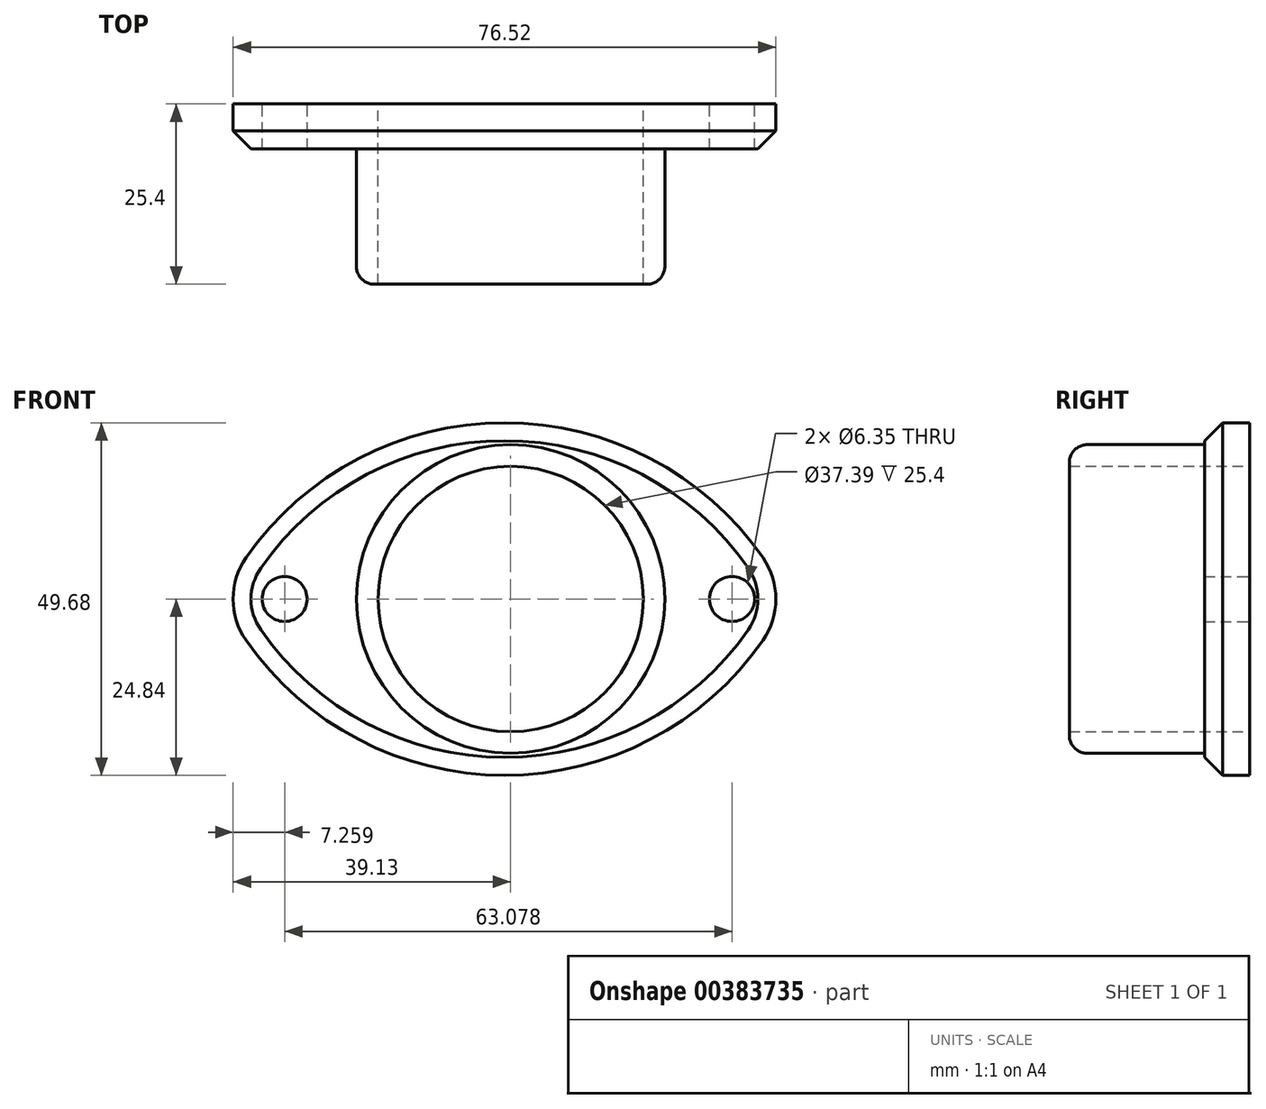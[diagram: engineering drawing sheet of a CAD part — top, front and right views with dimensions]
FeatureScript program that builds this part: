
annotation { "Feature Type Name" : "Feature", "Feature Type Description" : "" }
export const myFeature = defineFeature(function(context is Context, id is Id, definition is map)
    precondition{}
    {
        {
            var Q0;
            Q0=qCreatedBy(makeId("Front.planeOp"),FACE);
            var sketch = newSketch(context, id + "F0", { "sketchPlane" : qUnion([Q0])});
            skCircle(sketch, "E0", {"center": v(0, 0) * mm, "radius": 18.7 * mm});
            skArc(sketch, "E1", {"start": v(38.99, 0) * mm, "mid": v(-0.87, 24.84) * mm, "end": v(-40.73, 0) * mm});
            skArc(sketch, "E2.MirrorCS", {"start": v(38.99, 0) * mm, "mid": v(-0.87, -24.84) * mm, "end": v(-40.73, 0) * mm});
            skSolve(sketch);
        }
        {
            var Q0;
            Q0=makeQuery(id+"F0.imprint","IMPRINT",FACE,{"disambiguationData":[TD([[makeQuery(id+"F0.imprint","IMPRINT",EDGE,{"derivedFrom":sQuery(id+"F0.wireOp",EDGE,"E0")}),-1.0]])]});
            var sketch = newSketch(context, id + "F1", { "sketchPlane" : qUnion([Q0])});
            skCircle(sketch, "E3.0", {"center": v(0, 0) * mm, "radius": 21.74 * mm});
            skSolve(sketch);
        }
        {
            var Q0;
            Q0=makeQuery(id+"F1.imprint","IMPRINT",FACE,{"disambiguationData":[TD([[makeQuery(id+"F1.imprint","IMPRINT",EDGE,{"derivedFrom":sQuery(id+"F1.wireOp",EDGE,"E3.0")}),-1.0]])]});
            extrude(context, id + "F2", {"entities" : qUnion([Q0]), "depth" : 6.35 * mm});
        }
        {
            var Q0;
            Q0=makeQuery(id+"F1.imprint","IMPRINT",FACE,{"disambiguationData":[TD([[makeQuery(id+"F1.imprint","IMPRINT",EDGE,{"derivedFrom":sQuery(id+"F1.wireOp",EDGE,"E3.0")}),1.0]])]});
            extrude(context, id + "F3", {"entities" : qUnion([Q0]), "operationType" : NewBodyOperationType.ADD, "depth" : 25.4 * mm});
        }
        {
            var Q0;
            {var subQ0=sQuery(id+"F0.wireOp",EDGE,"E2.MirrorCS");var subQ1=sQuery(id+"F0.wireOp",EDGE,"E1");Q0=makeQuery(id+"F2.opExtrude","SWEPT_EDGE",EDGE,{"disambiguationData":[OSD([subQ1,subQ0]),TDD([makeQuery(id+"F1.imprint","INTERSECT",VERTEX,{"disambiguationData":[OD(1.0)],"derivedFrom":[makeQuery(id+"F0.imprint","IMPRINT",EDGE,{"derivedFrom":subQ1}),makeQuery(id+"F0.imprint","IMPRINT",EDGE,{"derivedFrom":subQ0})]})])]});}
            var Q1;
            {var subQ0=sQuery(id+"F0.wireOp",EDGE,"E2.MirrorCS");var subQ1=sQuery(id+"F0.wireOp",EDGE,"E1");Q1=makeQuery(id+"F2.opExtrude","SWEPT_EDGE",EDGE,{"disambiguationData":[OSD([subQ1,subQ0]),TDD([makeQuery(id+"F1.imprint","INTERSECT",VERTEX,{"disambiguationData":[OD(0.0)],"derivedFrom":[makeQuery(id+"F0.imprint","IMPRINT",EDGE,{"derivedFrom":subQ1}),makeQuery(id+"F0.imprint","IMPRINT",EDGE,{"derivedFrom":subQ0})]})])]});}
            fillet(context, id + "F4", {"entities" : qUnion([Q0, Q1]), "radius" : 10.16 * mm, "tangentPropagation" : true, "allowEdgeOverflow" : false});
        }
        {
            var Q0;
            Q0=qCreatedBy(makeId("Front.planeOp"),FACE);
            var sketch = newSketch(context, id + "F5", { "sketchPlane" : qUnion([Q0])});
            skCircle(sketch, "E4", {"center": v(-31.87, 0) * mm, "radius": 3.18 * mm});
            skCircle(sketch, "E5", {"center": v(31.2, 0) * mm, "radius": 3.18 * mm});
            skSolve(sketch);
        }
        {
            var Q0;
            Q0=sQuery(id+"F5.wireOp",VERTEX,"E4.center");
            var Q1;
            Q1=sQuery(id+"F5.wireOp",VERTEX,"E5.center");
            var Q2;
            Q2=makeQuery(id+"F2.opExtrude","SWEPT_BODY",BODY,{"disambiguationData":[OSD([sQuery(id+"F0.wireOp",EDGE,"E1"),sQuery(id+"F0.wireOp",EDGE,"E2.MirrorCS"),sQuery(id+"F1.wireOp",EDGE,"E3.0")])]});
            hole(context, id + "F6", {"style" : HoleStyle.SIMPLE, "endStyle" : HoleEndStyle.THROUGH, "oppositeDirection" : true, "holeDiameter" : 6.35 * mm, "isTappedThrough" : true, "tappedDepth" : 12.7 * mm, "tapClearance" : 3, "locations" : qUnion([Q0, Q1]), "scope" : qUnion([Q2])});
        }
        {
            var Q0;
            Q0=makeQuery(id+"F3.opExtrude","CAP_EDGE",EDGE,{"disambiguationData":[OSD([sQuery(id+"F1.wireOp",EDGE,"E3.0")])],"isStart":false});
            fillet(context, id + "F7", {"entities" : qUnion([Q0]), "radius" : 2.54 * mm, "tangentPropagation" : true, "allowEdgeOverflow" : false});
        }
        {
            var Q0;
            Q0=makeQuery(id+"F2.opExtrude","CAP_EDGE",EDGE,{"disambiguationData":[OSD([sQuery(id+"F0.wireOp",EDGE,"E1")])],"isStart":false});
            var Q1;
            {var subQ0=sQuery(id+"F0.wireOp",EDGE,"E2.MirrorCS");var subQ1=sQuery(id+"F0.wireOp",EDGE,"E1");Q1=makeQuery(id+"F4.opFillet","BLEND_EDGE",EDGE,{"blendedFrom":[makeQuery(id+"F2.opExtrude","SWEPT_EDGE",EDGE,{"disambiguationData":[OSD([subQ1,subQ0]),TDD([makeQuery(id+"F1.imprint","INTERSECT",VERTEX,{"disambiguationData":[OD(1.0)],"derivedFrom":[makeQuery(id+"F0.imprint","IMPRINT",EDGE,{"derivedFrom":subQ1}),makeQuery(id+"F0.imprint","IMPRINT",EDGE,{"derivedFrom":subQ0})]})])]}),makeQuery(id+"F2.opExtrude","CAP_FACE",FACE,{"disambiguationData":[OSD([subQ1,subQ0,sQuery(id+"F1.wireOp",EDGE,"E3.0")])],"isStart":false})],"blendedInto":[makeQuery(id+"F2.opExtrude","CAP_FACE",FACE,{"disambiguationData":[OSD([subQ1,subQ0,sQuery(id+"F1.wireOp",EDGE,"E3.0")])],"isStart":false})]});}
            var Q2;
            Q2=makeQuery(id+"F2.opExtrude","CAP_EDGE",EDGE,{"disambiguationData":[OSD([sQuery(id+"F0.wireOp",EDGE,"E2.MirrorCS")])],"isStart":false});
            var Q3;
            {var subQ0=sQuery(id+"F0.wireOp",EDGE,"E2.MirrorCS");var subQ1=sQuery(id+"F0.wireOp",EDGE,"E1");Q3=makeQuery(id+"F4.opFillet","BLEND_EDGE",EDGE,{"blendedFrom":[makeQuery(id+"F2.opExtrude","SWEPT_EDGE",EDGE,{"disambiguationData":[OSD([subQ1,subQ0]),TDD([makeQuery(id+"F1.imprint","INTERSECT",VERTEX,{"disambiguationData":[OD(0.0)],"derivedFrom":[makeQuery(id+"F0.imprint","IMPRINT",EDGE,{"derivedFrom":subQ1}),makeQuery(id+"F0.imprint","IMPRINT",EDGE,{"derivedFrom":subQ0})]})])]}),makeQuery(id+"F2.opExtrude","CAP_FACE",FACE,{"disambiguationData":[OSD([subQ1,subQ0,sQuery(id+"F1.wireOp",EDGE,"E3.0")])],"isStart":false})],"blendedInto":[makeQuery(id+"F2.opExtrude","CAP_FACE",FACE,{"disambiguationData":[OSD([subQ1,subQ0,sQuery(id+"F1.wireOp",EDGE,"E3.0")])],"isStart":false})]});}
            chamfer(context, id + "F8", {"entities" : qUnion([Q0, Q1, Q2, Q3]), "width" : 2.54 * mm, "tangentPropagation" : true});
        }
    });
